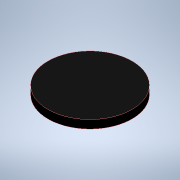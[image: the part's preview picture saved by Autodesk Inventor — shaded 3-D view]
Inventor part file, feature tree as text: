
AUTODESK INVENTOR PART (.ipt)
format: ipt  version: 2022 (Build 260153000, 153)  size: 100,352 bytes
history: native  units: mm
features: extrude x1, sketch x1
ambient origin geometry x8: Origin, YZ Plane, XZ Plane, XY Plane, X Axis, Y Axis, Z Axis, Center Point
bodies: Solid1 (feature_tree)
feature tree (2):
  extrude  "Extrusion1"  [1 undecoded]
  sketch  "Sketch1"  dims[d0=1.0mm d1=0.0mm]
note: 1 required parameter value undecoded (feature->parameter linkage not recoverable at this tier; creation-order binding heuristic only, values carry confidence <= 0.55)
